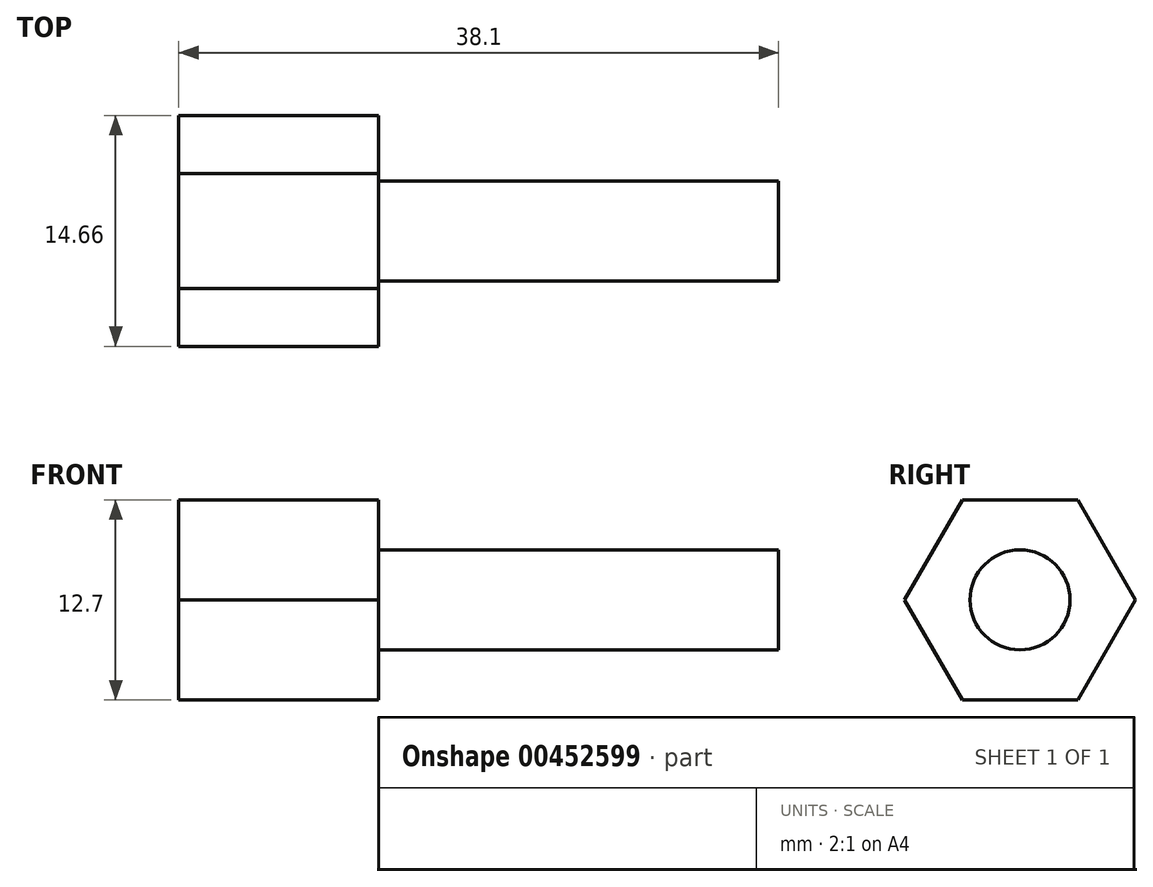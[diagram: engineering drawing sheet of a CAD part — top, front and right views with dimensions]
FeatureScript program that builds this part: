
annotation { "Feature Type Name" : "Feature", "Feature Type Description" : "" }
export const myFeature = defineFeature(function(context is Context, id is Id, definition is map)
    precondition{}
    {
        {
            var Q0;
            Q0=qCreatedBy(makeId("Right.planeOp"),FACE);
            var sketch = newSketch(context, id + "F0", { "sketchPlane" : qUnion([Q0])});
            skCircle(sketch, "E0.cCircle", {"center": v(0, 0) * mm, "radius": 6.35 * mm, "construction": true});
            skLineSegment(sketch, "E0.0", {"start": v(3.67, 6.35) * mm, "end": v(7.33, 0) * mm});
            skLineSegment(sketch, "E0.1", {"start": v(7.33, 0) * mm, "end": v(3.67, -6.35) * mm});
            skLineSegment(sketch, "E0.2", {"start": v(3.67, -6.35) * mm, "end": v(-3.67, -6.35) * mm});
            skLineSegment(sketch, "E0.3", {"start": v(-3.67, -6.35) * mm, "end": v(-7.33, 0) * mm});
            skLineSegment(sketch, "E0.4", {"start": v(-7.33, 0) * mm, "end": v(-3.67, 6.35) * mm});
            skLineSegment(sketch, "E0.5", {"start": v(-3.67, 6.35) * mm, "end": v(3.67, 6.35) * mm});
            skPoint(sketch, "E0.0.midPoint", {"position": v(5.5, 3.18) * mm});
            skSolve(sketch);
        }
        {
            var Q0;
            Q0 = qSketchRegion(id + "F0", true);
            extrude(context, id + "F1", {"entities" : qUnion([Q0]), "depth" : 38.1 * mm, "offsetDistance" : 25.4 * mm});
        }
        {
            var Q0;
            Q0=makeQuery(id+"F1.opExtrude","CAP_FACE",FACE,{"disambiguationData":[OSD([sQuery(id+"F0.wireOp",EDGE,"E0.0"),sQuery(id+"F0.wireOp",EDGE,"E0.1"),sQuery(id+"F0.wireOp",EDGE,"E0.2"),sQuery(id+"F0.wireOp",EDGE,"E0.3"),sQuery(id+"F0.wireOp",EDGE,"E0.4"),sQuery(id+"F0.wireOp",EDGE,"E0.5")])],"isStart":false});
            var sketch = newSketch(context, id + "F2", { "sketchPlane" : qUnion([Q0])});
            skCircle(sketch, "E1", {"center": v(0, 0) * mm, "radius": 3.18 * mm});
            skSolve(sketch);
        }
        {
            var Q0;
            Q0=makeQuery(id+"F2.imprint","IMPRINT",FACE,{"disambiguationData":[TD([[makeQuery(id+"F2.imprint","IMPRINT",EDGE,{"derivedFrom":sQuery(id+"F2.wireOp",EDGE,"E1")}),-1.0]])]});
            extrude(context, id + "F3", {"entities" : qUnion([Q0]), "operationType" : NewBodyOperationType.REMOVE, "oppositeDirection" : true, "depth" : 25.4 * mm, "offsetDistance" : 25.4 * mm});
        }
    });
